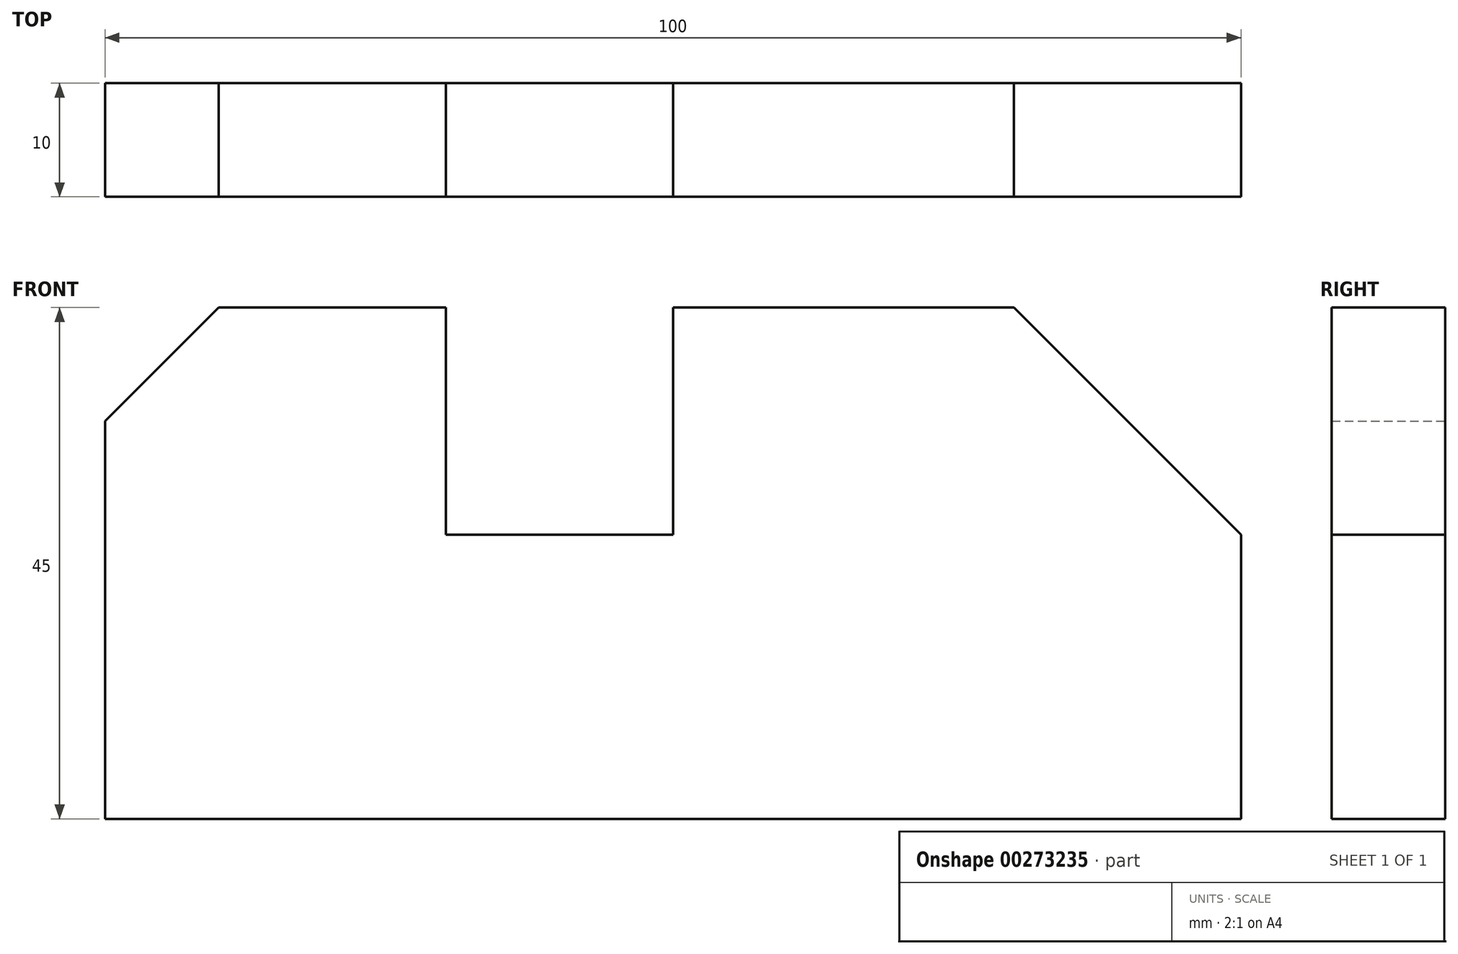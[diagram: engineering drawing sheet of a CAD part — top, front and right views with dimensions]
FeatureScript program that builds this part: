
annotation { "Feature Type Name" : "Feature", "Feature Type Description" : "" }
export const myFeature = defineFeature(function(context is Context, id is Id, definition is map)
    precondition{}
    {
        {
            var Q0;
            Q0=qCreatedBy(makeId("Front.planeOp"),FACE);
            var sketch = newSketch(context, id + "F0", { "sketchPlane" : qUnion([Q0])});
            skLineSegment(sketch, "E0", {"start": v(0, 0) * mm, "end": v(100, 0) * mm});
            skLineSegment(sketch, "E1", {"start": v(0, 35) * mm, "end": v(10, 45) * mm});
            skLineSegment(sketch, "E2", {"start": v(10, 45) * mm, "end": v(30, 45) * mm});
            skLineSegment(sketch, "E3", {"start": v(30, 45) * mm, "end": v(30, 25) * mm});
            skLineSegment(sketch, "E4", {"start": v(30, 25) * mm, "end": v(50, 25) * mm});
            skLineSegment(sketch, "E5", {"start": v(50, 25) * mm, "end": v(50, 45) * mm});
            skLineSegment(sketch, "E6", {"start": v(50, 45) * mm, "end": v(80, 45) * mm});
            skLineSegment(sketch, "E7", {"start": v(80, 45) * mm, "end": v(100, 25) * mm});
            skLineSegment(sketch, "E8", {"start": v(100, 25) * mm, "end": v(100, 0) * mm});
            skLineSegment(sketch, "E9", {"start": v(0, 35) * mm, "end": v(0, 0) * mm});
            skSolve(sketch);
        }
        {
            var Q0;
            Q0=makeQuery(id+"F0.imprint","IMPRINT",FACE,{"disambiguationData":[TD([[makeQuery(id+"F0.imprint","IMPRINT",EDGE,{"derivedFrom":sQuery(id+"F0.wireOp",EDGE,"E0")}),1.0]])]});
            extrude(context, id + "F1", {"entities" : qUnion([Q0]), "depth" : 10 * mm});
        }
    });
